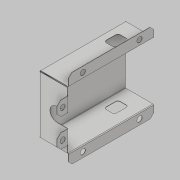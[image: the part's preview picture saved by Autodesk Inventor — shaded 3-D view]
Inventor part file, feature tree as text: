
AUTODESK INVENTOR PART (.ipt)
format: ipt  version: 2019 (Build 230136000, 136)  size: 413,184 bytes
history: native  units: mm
features: sketch x8, sheet_metal_op x7, other x2, fillet x2, chamfer x1, extrude x1, plane x1, mirror x1
ambient origin geometry x8: Origin, YZ Plane, XZ Plane, XY Plane, X Axis, Y Axis, Z Axis, Center Point
bodies: Solid1 (feature_tree)
feature tree (23):
  sheet_metal_op  "Face1"
  sheet_metal_op  "Fold2"
  sheet_metal_op  "Fold3"
  sheet_metal_op  "Fold4"
  sheet_metal_op  "Fold5"
  sheet_metal_op  "Fold6"
  sheet_metal_op  "Fold7"
  chamfer  "Corner Round1"
  other  "Corner Chamfer1"
  extrude  "Extrusion1"  Depth=12.0mm
  fillet  "Fillet1"  Radius=5.5mm
  fillet  "Fillet2"  Radius=5.5mm
  plane  "Work Plane1"
  mirror  "Mirror1"
  sketch  "Sketch1"  dims[d0=8.0mm d1=12.0mm d2=5.5mm d4=5.5mm]
  other  "Plate1"
  sketch  "Sketch4"  dims[d5=12.0mm]
  sketch  "Sketch5"  dims[d6=3.5mm]
  sketch  "Sketch6"  dims[d7=2.0mm]
  sketch  "Sketch7"  dims[d8=8.0mm]
  sketch  "Sketch8"  dims[d9=4.0mm]
  sketch  "Sketch9"  dims[d10=1.5mm]
  sketch  "Sketch10"  dims[d11=2.0mm d12=2.0mm d13=1.0mm d14=1.5mm d15=0.75mm d16=2.0mm d19=0.75mm d20=0.75mm d21=0.05mm d30=12.0mm d31=0.057mm d32=0.05mm d33=0.025mm d34=0.1mm d35=0.05mm d36=90.0deg d37=0.05mm d38=8.0mm d39=0.057mm d40=0.05mm d41=0.025mm d42=0.1mm d43=0.05mm d44=90.0deg d45=0.05mm d46=12.0mm d47=1.5mm d48=0.05mm d49=0.025mm d50=0.1mm d51=0.05mm d52=90.0deg d53=0.05mm d54=0.05mm d55=0.025mm d56=0.1mm d57=0.05mm d58=90.0deg d59=0.05mm d60=12.0mm d61=0.057mm d62=0.05mm d63=0.025mm d64=0.1mm d65=0.05mm d66=90.0deg d67=0.05mm d68=12.0mm d69=1.5mm d70=0.05mm d71=0.025mm d72=0.1mm d73=0.05mm d74=90.0deg d75=0.05mm d76=0.35mm d77=0.5mm d78=6.0mm d79=45.0deg d80=12.0mm d81=2.0mm d82=0.75mm d83=0.75mm d84=0.35mm d85=0.0mm d86=0.25mm d87=0.1mm d88=1.5mm d89=0.75mm d90=0.75mm d91=0.75mm d92=0.75mm d93=0.75mm d94=0.75mm d95=1.75mm d96=1.75mm d97=1.75mm d98=-4.1mm]
